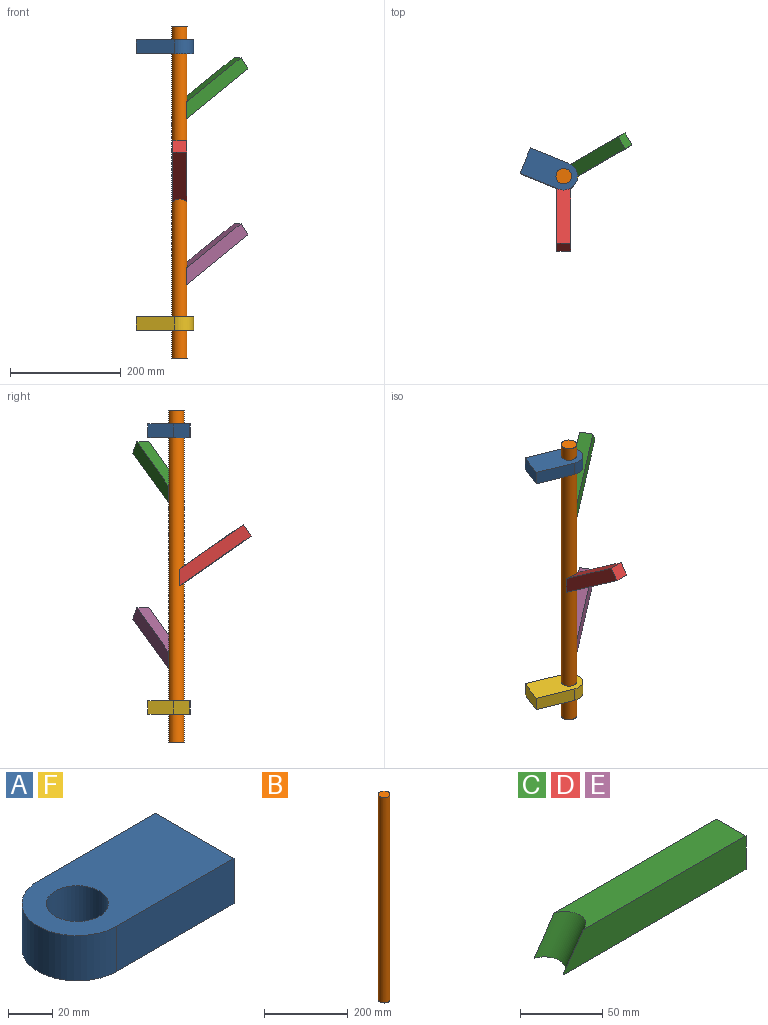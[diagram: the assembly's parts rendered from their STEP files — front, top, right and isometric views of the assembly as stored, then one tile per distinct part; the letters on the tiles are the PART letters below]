
ASSEMBLY  parts=6 mates=3
PART A: 7 faces, bbox 100x50x25 mm
  f0: plane 75x25mm, normal (0,1,0), area 1875mm2, adj f1,f3,f5,f6
  f1: cylinder r=25mm len=50mm, axis (0,0,-1), area 1963.5mm2, adj f0,f2,f5,f6
  f2: plane 75x25mm, normal (0,-1,0), area 1875mm2, adj f1,f3,f5,f6
  f3: plane 50x25mm, normal (1,0,0), area 1250mm2, adj f0,f2,f5,f6
  f4: cylinder r=14mm len=28mm, axis (0,0,-1), area 2199.1mm2, adj f5,f6
  f5: plane 100x50mm, normal (0,0,1), area 4116mm2, adj f0,f1,f2,f3,f4
  f6: plane 100x50mm, normal (0,0,-1), area 4116mm2, adj f0,f1,f2,f3,f4
PART B: 3 faces, bbox 28x28x600 mm
  f0: cylinder r=14mm len=600mm, axis (0,0,-1), area 52778.8mm2, adj f1,f2
  f1: plane 28x28mm, normal (0,0,1), area 615.8mm2, adj f0
  f2: plane 28x28mm, normal (0,0,-1), area 615.8mm2, adj f0
PART C: 6 faces, bbox 157.3x25x33.8 mm
  f0: plane 139.8x25mm, normal (0,0,1), area 3327.1mm2, adj f1,f2,f3,f5
  f1: plane 157.3x25mm, normal (0,-1,0), area 3713.8mm2, adj f0,f2,f4,f5
  f2: plane 25x25mm, normal (1,0,0), area 625mm2, adj f0,f1,f3,f4
  f3: plane 157.3x25mm, normal (0,1,0), area 3713.8mm2, adj f0,f2,f4,f5
  f4: plane 157.3x25mm, normal (0,0,-1), area 3764.7mm2, adj f1,f2,f3,f5
  f5: cylinder r=14mm len=33.84mm, axis (-0.57,0,-0.82), area 943.1mm2, adj f0,f1,f3,f4
PART D: same geometry as C
PART E: same geometry as C
PART F: same geometry as A
PLACE A rot(axis=(0,0,1),158deg) t=(-151.45,78.96,130.35)mm
PLACE B rot(axis=(0,0,-1),180deg) t=(-128.27,69.6,-419.65)mm fixed
PLACE C rot(axis=(0.2,-0.75,0.63),45.8deg) t=(-69.74,103.39,55.3)mm
PLACE D rot(axis=(-0.29,-0.29,-0.91),95.2deg) t=(-128.27,2.02,-94.7)mm
PLACE E rot(axis=(0.2,-0.75,0.63),45.8deg) t=(-69.74,103.39,-244.7)mm
PLACE F rot(axis=(0,0,1),158deg) t=(-151.45,78.96,-369.65)mm
MATE revolute B.f0 <-> C.f5  axis (0,0,1) through (-128.27,69.6,180.35)mm
MATE cylindrical A.f4 <-> B.f0  axis (0,0,1) through (-128.27,69.6,155.35)mm
MATE revolute B.f0 <-> D.f5  axis (0,0,1) through (-128.27,69.6,180.35)mm
